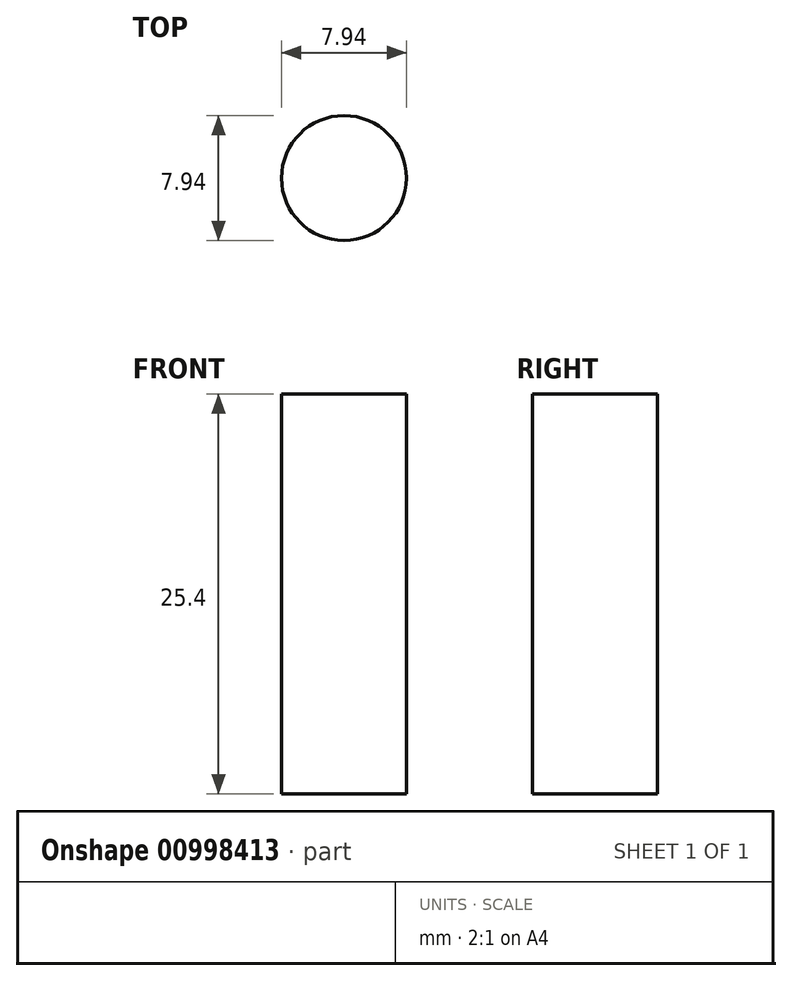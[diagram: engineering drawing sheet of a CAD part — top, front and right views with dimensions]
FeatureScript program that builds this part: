
annotation { "Feature Type Name" : "Feature", "Feature Type Description" : "" }
export const myFeature = defineFeature(function(context is Context, id is Id, definition is map)
    precondition{}
    {
        {
            var Q0;
            Q0=qCreatedBy(makeId("Top.planeOp"),FACE);
            var sketch = newSketch(context, id + "F0", { "sketchPlane" : qUnion([Q0])});
            skCircle(sketch, "E0", {"center": v(0, 0) * mm, "radius": 3.97 * mm});
            skSolve(sketch);
        }
        {
            var Q0;
            Q0=makeQuery(id+"F0.imprint","IMPRINT",FACE,{"disambiguationData":[TD([[makeQuery(id+"F0.imprint","IMPRINT",EDGE,{"derivedFrom":sQuery(id+"F0.wireOp",EDGE,"E0")}),1.0]])]});
            extrude(context, id + "F1", {"entities" : qUnion([Q0]), "depth" : 25.4 * mm, "offsetDistance" : 25.4 * mm});
        }
    });
